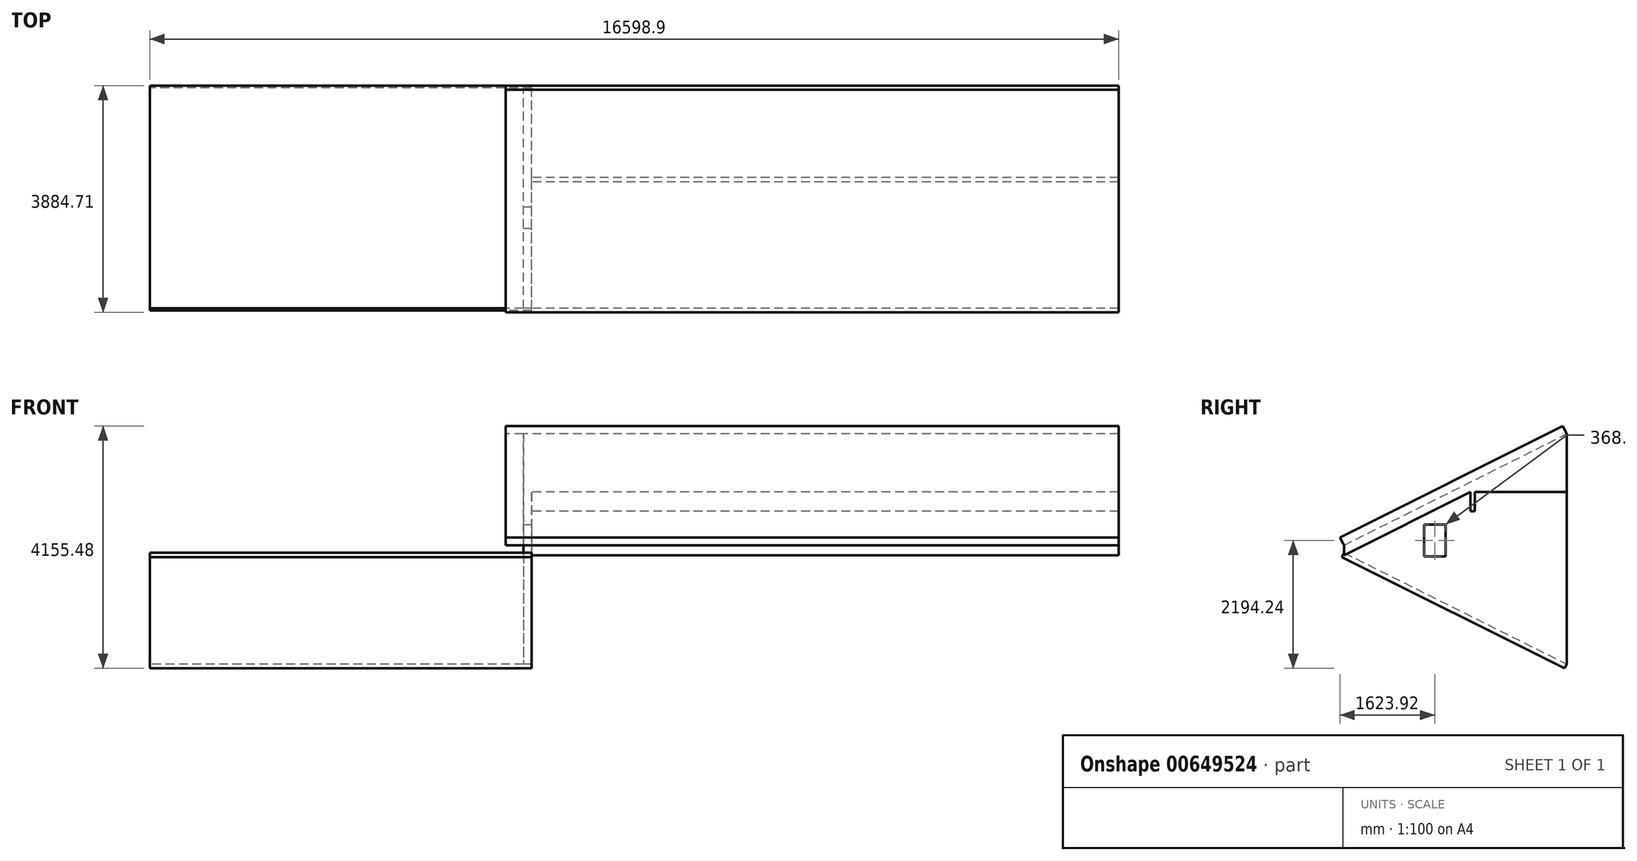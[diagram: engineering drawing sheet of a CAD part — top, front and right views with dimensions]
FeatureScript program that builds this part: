
annotation { "Feature Type Name" : "Feature", "Feature Type Description" : "" }
export const myFeature = defineFeature(function(context is Context, id is Id, definition is map)
    precondition{}
    {
        {
            var Q0;
            Q0=qCreatedBy(makeId("Right.planeOp"),FACE);
            var sketch = newSketch(context, id + "F0", { "sketchPlane" : qUnion([Q0])});
            skLineSegment(sketch, "E0", {"start": v(-1218.54, 872.31) * mm, "end": v(2598, -1036.37) * mm});
            skLineSegment(sketch, "E1", {"start": v(2598, -1036.37) * mm, "end": v(-1756.95, -1036.37) * mm, "construction": true});
            skLineSegment(sketch, "E2", {"start": v(-1218.54, 872.31) * mm, "end": v(-1181.13, 947.12) * mm});
            skLineSegment(sketch, "E3", {"start": v(-1181.13, 947.12) * mm, "end": v(2635.4, -961.56) * mm});
            skLineSegment(sketch, "E4", {"start": v(2598, -1036.37) * mm, "end": v(2635.4, -961.56) * mm});
            skPoint(sketch, "E5", {"position": v(1378.8, -1036.37) * mm});
            skSolve(sketch);
        }
        {
            var Q0;
            Q0 = qSketchRegion(id + "F0", true);
            extrude(context, id + "F1", {"entities" : qUnion([Q0]), "depth" : 6400.8 * mm, "offsetDistance" : 25.4 * mm});
        }
        {
            var Q0;
            Q0=makeQuery(id+"F1.opExtrude","CAP_FACE",FACE,{"disambiguationData":[OSD([sQuery(id+"F0.wireOp",EDGE,"E0"),sQuery(id+"F0.wireOp",EDGE,"E2"),sQuery(id+"F0.wireOp",EDGE,"E3"),sQuery(id+"F0.wireOp",EDGE,"E4")])],"isStart":false});
            var sketch = newSketch(context, id + "F2", { "sketchPlane" : qUnion([Q0])});
            skLineSegment(sketch, "E6", {"start": v(-1181.13, 947.12) * mm, "end": v(-1181.13, 1074.12) * mm});
            skLineSegment(sketch, "E7", {"start": v(-1181.13, 1074.12) * mm, "end": v(2635.4, 2982.8) * mm});
            skLineSegment(sketch, "E8", {"start": v(-1181.13, 1074.12) * mm, "end": v(-825.53, 1074.12) * mm, "construction": true});
            skLineSegment(sketch, "E9", {"start": v(2635.4, 2982.8) * mm, "end": v(2635.4, -961.56) * mm});
            skLineSegment(sketch, "E10", {"start": v(-1181.13, 947.12) * mm, "end": v(-1218.54, 872.31) * mm});
            skLineSegment(sketch, "E11", {"start": v(-1218.54, 872.31) * mm, "end": v(2598, -1036.37) * mm});
            skLineSegment(sketch, "E12", {"start": v(2598, -1036.37) * mm, "end": v(2635.4, -961.56) * mm});
            skSolve(sketch);
        }
        {
            var Q0;
            Q0 = qSketchRegion(id + "F2", true);
            extrude(context, id + "F3", {"entities" : qUnion([Q0]), "operationType" : NewBodyOperationType.ADD, "depth" : 139.7 * mm, "offsetDistance" : 25.4 * mm});
        }
        {
            var Q0;
            Q0=makeQuery(id+"F3.opExtrude","CAP_FACE",FACE,{"disambiguationData":[OSD([sQuery(id+"F2.wireOp",EDGE,"E6"),sQuery(id+"F2.wireOp",EDGE,"E7"),sQuery(id+"F2.wireOp",EDGE,"E9"),sQuery(id+"F2.wireOp",EDGE,"E10"),sQuery(id+"F2.wireOp",EDGE,"E11"),sQuery(id+"F2.wireOp",EDGE,"E12")])],"isStart":false});
            var sketch = newSketch(context, id + "F4", { "sketchPlane" : qUnion([Q0])});
            skLineSegment(sketch, "E13", {"start": v(-1181.13, 1074.12) * mm, "end": v(-1249.3, 1210.43) * mm});
            skLineSegment(sketch, "E14", {"start": v(-1249.3, 1210.43) * mm, "end": v(2567.24, 3119.1) * mm});
            skLineSegment(sketch, "E15", {"start": v(2635.4, 2982.8) * mm, "end": v(2567.24, 3119.1) * mm});
            skSolve(sketch);
        }
        {
            var Q0;
            Q0=makeQuery(id+"F4.imprint","IMPRINT",FACE,{"disambiguationData":[TD([[makeQuery(id+"F4.imprint","IMPRINT",EDGE,{"derivedFrom":sQuery(id+"F4.wireOp",EDGE,"E13")}),-1.0]])]});
            extrude(context, id + "F5", {"entities" : qUnion([Q0]), "operationType" : NewBodyOperationType.ADD, "depth" : 10058.4 * mm, "offsetDistance" : 25.4 * mm, "hasSecondDirection" : true, "secondDirectionOppositeDirection" : true, "secondDirectionDepth" : 444.5 * mm});
        }
        {
            var Q0;
            Q0=makeQuery(id+"F3.opExtrude","CAP_FACE",FACE,{"disambiguationData":[OSD([sQuery(id+"F2.wireOp",EDGE,"E6"),sQuery(id+"F2.wireOp",EDGE,"E7"),sQuery(id+"F2.wireOp",EDGE,"E9"),sQuery(id+"F2.wireOp",EDGE,"E10"),sQuery(id+"F2.wireOp",EDGE,"E11"),sQuery(id+"F2.wireOp",EDGE,"E12")])],"isStart":false});
            var sketch = newSketch(context, id + "F6", { "sketchPlane" : qUnion([Q0])});
            skLineSegment(sketch, "E16", {"start": v(-1181.13, 1074.12) * mm, "end": v(-1181.13, 903.73) * mm});
            skLineSegment(sketch, "E17", {"start": v(-1181.13, 903.73) * mm, "end": v(2635.4, 2812.4) * mm});
            skLineSegment(sketch, "E18", {"start": v(2635.4, 2812.4) * mm, "end": v(2635.4, 2982.8) * mm});
            skLineSegment(sketch, "E19", {"start": v(2635.4, 2982.8) * mm, "end": v(-1181.13, 1074.12) * mm});
            skSolve(sketch);
        }
        {
            var Q0;
            Q0=makeQuery(id+"F6.imprint","IMPRINT",FACE,{"disambiguationData":[TD([[makeQuery(id+"F6.imprint","IMPRINT",EDGE,{"derivedFrom":sQuery(id+"F6.wireOp",EDGE,"E19")}),-1.0]])]});
            var sketch = newSketch(context, id + "F7", { "sketchPlane" : qUnion([Q0])});
            skLineSegment(sketch, "E20.bottom", {"start": v(190.47, 1430.92) * mm, "end": v(558.77, 1430.92) * mm});
            skLineSegment(sketch, "E20.top", {"start": v(190.47, 884.82) * mm, "end": v(558.77, 884.82) * mm});
            skLineSegment(sketch, "E20.left", {"start": v(190.47, 1430.92) * mm, "end": v(190.47, 884.82) * mm});
            skLineSegment(sketch, "E20.right", {"start": v(558.77, 1430.92) * mm, "end": v(558.77, 884.82) * mm});
            skLineSegment(sketch, "E21", {"start": v(190.47, 1430.92) * mm, "end": v(190.47, 1589.67) * mm, "construction": true});
            skSolve(sketch);
        }
        {
            var Q0;
            Q0 = qSketchRegion(id + "F6", true);
            extrude(context, id + "F8", {"entities" : qUnion([Q0]), "operationType" : NewBodyOperationType.ADD, "depth" : 10058.4 * mm, "offsetDistance" : 25.4 * mm});
        }
        {
            var Q0;
            Q0 = qSketchRegion(id + "F7", true);
            extrude(context, id + "F9", {"entities" : qUnion([Q0]), "operationType" : NewBodyOperationType.REMOVE, "endBound" : BoundingType.THROUGH_ALL, "oppositeDirection" : true, "depth" : 25.4 * mm, "offsetDistance" : 25.4 * mm});
        }
        {
            var Q0;
            Q0=makeQuery(id+"F3.opExtrude","CAP_FACE",FACE,{"disambiguationData":[OSD([sQuery(id+"F2.wireOp",EDGE,"E6"),sQuery(id+"F2.wireOp",EDGE,"E7"),sQuery(id+"F2.wireOp",EDGE,"E9"),sQuery(id+"F2.wireOp",EDGE,"E10"),sQuery(id+"F2.wireOp",EDGE,"E11"),sQuery(id+"F2.wireOp",EDGE,"E12")])],"isStart":false});
            var sketch = newSketch(context, id + "F10", { "sketchPlane" : qUnion([Q0])});
            skLineSegment(sketch, "E22.bottom", {"start": v(987.4, 1988.22) * mm, "end": v(1063.6, 1988.22) * mm, "construction": true});
            skLineSegment(sketch, "E22.top", {"start": v(987.4, 1658.02) * mm, "end": v(1063.6, 1658.02) * mm});
            skLineSegment(sketch, "E22.left", {"start": v(987.4, 1988.22) * mm, "end": v(987.4, 1658.02) * mm});
            skLineSegment(sketch, "E22.right", {"start": v(1063.6, 1988.22) * mm, "end": v(1063.6, 1658.02) * mm});
            skLineSegment(sketch, "E23", {"start": v(1063.6, 1988.22) * mm, "end": v(2635.4, 1988.22) * mm});
            skLineSegment(sketch, "E24", {"start": v(2635.4, 1988.22) * mm, "end": v(2635.4, 2812.4) * mm});
            skLineSegment(sketch, "E25", {"start": v(2635.4, 2812.4) * mm, "end": v(987.4, 1988.22) * mm});
            skSolve(sketch);
        }
        {
            var Q0;
            Q0 = qSketchRegion(id + "F10", true);
            extrude(context, id + "F11", {"entities" : qUnion([Q0]), "operationType" : NewBodyOperationType.ADD, "depth" : 10058.4 * mm, "offsetDistance" : 25.4 * mm});
        }
    });
